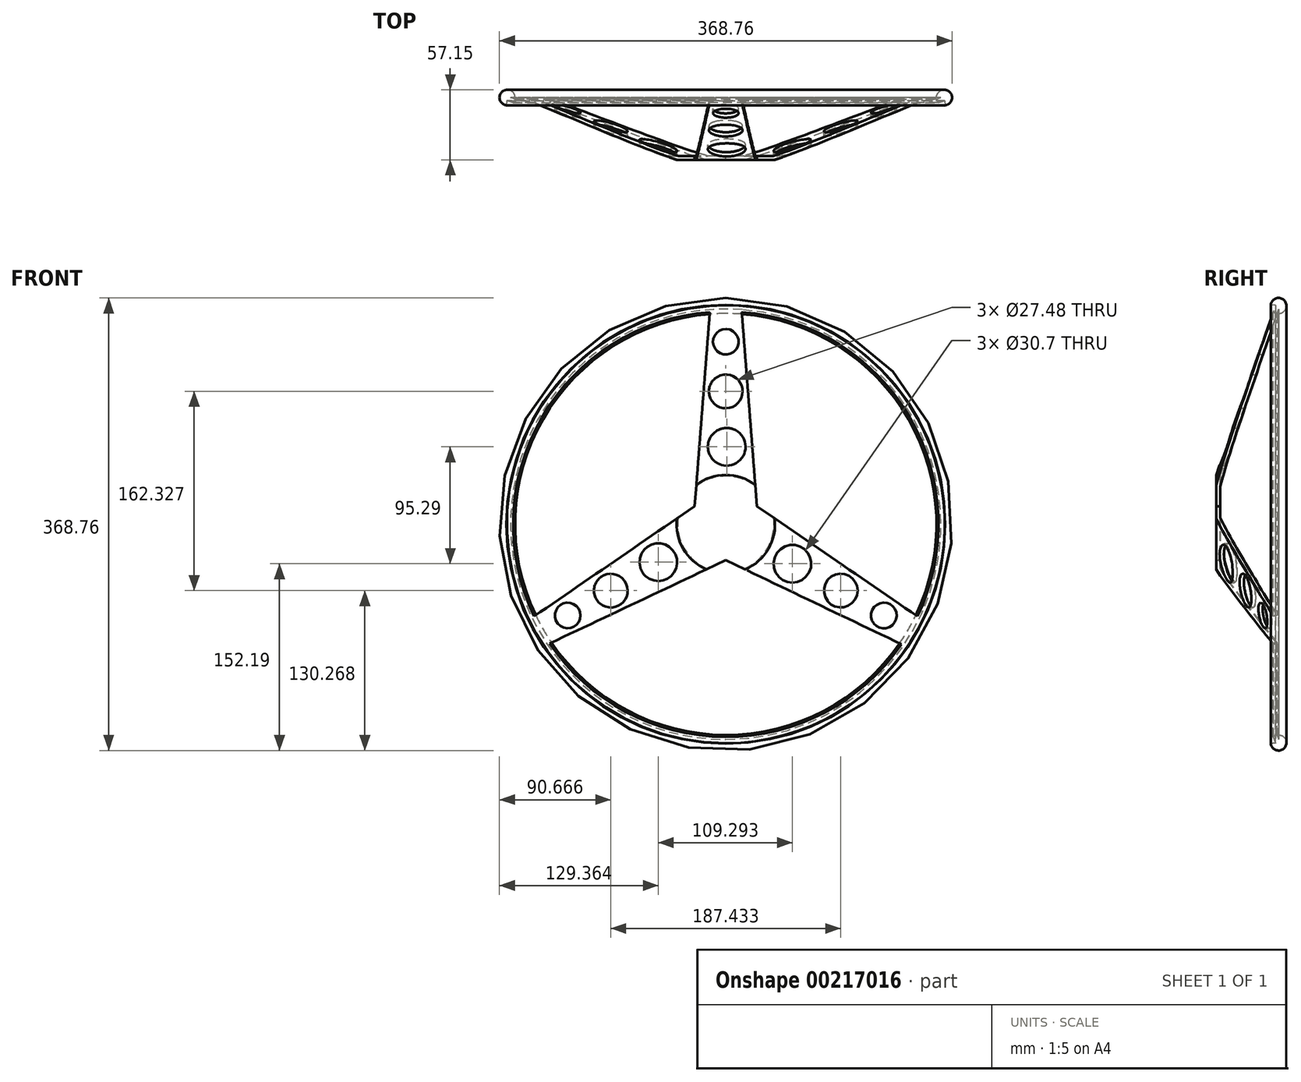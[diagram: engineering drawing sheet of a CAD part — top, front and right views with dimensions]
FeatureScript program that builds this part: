
annotation { "Feature Type Name" : "Feature", "Feature Type Description" : "" }
export const myFeature = defineFeature(function(context is Context, id is Id, definition is map)
    precondition{}
    {
        {
            var Q0;
            Q0=qCreatedBy(makeId("Front.planeOp"),FACE);
            var sketch = newSketch(context, id + "F0", { "sketchPlane" : qUnion([Q0])});
            skCircle(sketch, "E0", {"center": v(0, 0) * mm, "radius": 177.8 * mm});
            skLineSegment(sketch, "E1.1", {"start": v(139.7, -109.99) * mm, "end": v(141.28, -110.9) * mm});
            skLineSegment(sketch, "E2", {"start": v(-159.95, -77.64) * mm, "end": v(-25.4, 14.66) * mm});
            skLineSegment(sketch, "E3", {"start": v(-147.63, -99.09) * mm, "end": v(0, -29.33) * mm});
            skPoint(sketch, "E3.startSnap0", {"position": v(-147.63, -99.9) * mm});
            skLineSegment(sketch, "E4", {"start": v(159.95, -77.64) * mm, "end": v(25.4, 14.66) * mm});
            skLineSegment(sketch, "E5", {"start": v(0, -29.33) * mm, "end": v(147.22, -99.7) * mm});
            skLineSegment(sketch, "E6", {"start": v(-12.7, 177.8) * mm, "end": v(-25.4, 14.66) * mm});
            skLineSegment(sketch, "E7", {"start": v(12.74, 177.34) * mm, "end": v(25.4, 14.66) * mm});
            skPoint(sketch, "E8.1.end.orphan", {"position": v(-25.4, 177.8) * mm});
            skPoint(sketch, "E9.orphan", {"position": v(25.4, 177.8) * mm});
            skPoint(sketch, "E10.start.orphan", {"position": v(12.7, 177.8) * mm});
            skPoint(sketch, "E11.1.end.orphan", {"position": v(166.68, -66.9) * mm});
            skPoint(sketch, "E12.orphan", {"position": v(160.33, -77.9) * mm});
            skPoint(sketch, "E13.orphan", {"position": v(147.63, -99.9) * mm});
            skPoint(sketch, "E1.0.end.orphan", {"position": v(-141.28, -110.9) * mm});
            skPoint(sketch, "E14.orphan", {"position": v(-160.33, -77.9) * mm});
            skPoint(sketch, "E8.0.end.orphan", {"position": v(-166.68, -66.9) * mm});
            skPoint(sketch, "E15.end.orphan", {"position": v(0, 177.8) * mm});
            skPoint(sketch, "E16.end.orphan", {"position": v(-153.98, -88.9) * mm});
            skPoint(sketch, "E17.end.orphan", {"position": v(153.98, -88.9) * mm});
            skCircle(sketch, "E18", {"center": v(0, 0) * mm, "radius": 29.33 * mm});
            skSolve(sketch);
        }
        {
            var Q0;
            {var subQ0=sQuery(id+"F0.wireOp",EDGE,"E2");Q0=makeQuery(id+"F0.imprint","IMPRINT",FACE,{"disambiguationData":[TD([[makeQuery(id+"F0.imprint","IMPRINT",EDGE,{"derivedFrom":subQ0}),-1.0]])]});}
            var Q1;
            {var subQ0=sQuery(id+"F0.wireOp",EDGE,"E7");Q1=makeQuery(id+"F0.imprint","IMPRINT",FACE,{"disambiguationData":[TD([[makeQuery(id+"F0.imprint","IMPRINT",EDGE,{"derivedFrom":subQ0}),-1.0]])]});}
            var Q2;
            {var subQ0=sQuery(id+"F0.wireOp",EDGE,"E4");Q2=makeQuery(id+"F0.imprint","IMPRINT",FACE,{"disambiguationData":[TD([[makeQuery(id+"F0.imprint","IMPRINT",EDGE,{"derivedFrom":subQ0}),1.0]])]});}
            var Q3;
            {var subQ0=sQuery(id+"F0.wireOp",EDGE,"E18");var subQ1=makeQuery(id+"F0.imprint","INTERSECT",VERTEX,{"derivedFrom":[sQuery(id+"F0.wireOp",EDGE,"E2"),sQuery(id+"F0.wireOp",EDGE,"E6"),subQ0]});Q3=makeQuery(id+"F0.imprint","IMPRINT",FACE,{"disambiguationData":[TD([[makeQuery(id+"F0.imprint","IMPRINT",EDGE,{"disambiguationData":[TD([[subQ1,1.0]])],"derivedFrom":subQ0}),1.0]])]});}
            extrude(context, id + "F1", {"entities" : qUnion([Q0, Q1, Q2, Q3]), "depth" : 50.8 * mm});
        }
        {
            var Q0;
            Q0=qCreatedBy(makeId("Right.planeOp"),FACE);
            var sketch = newSketch(context, id + "F2", { "sketchPlane" : qUnion([Q0])});
            skCircle(sketch, "E19", {"center": v(0, 178.03) * mm, "radius": 6.35 * mm});
            skSolve(sketch);
        }
        {
            var Q0;
            Q0 = qSketchRegion(id + "F2", true);
            var Q1;
            {var subQ0=sQuery(id+"F0.wireOp",EDGE,"E0");Q1=makeQuery(id+"F1.opExtrude","SWEPT_FACE",FACE,{"disambiguationData":[OSD([subQ0]),TDD([makeQuery(id+"F0.imprint","IMPRINT",EDGE,{"disambiguationData":[TD([[makeQuery(id+"F0.imprint","INTERSECT",VERTEX,{"derivedFrom":[subQ0,sQuery(id+"F0.wireOp",EDGE,"E7")]}),-1.0]])],"derivedFrom":subQ0})])]});}
            revolve(context, id + "F3", {"operationType" : NewBodyOperationType.ADD, "entities" : qUnion([Q0]), "axis" : qUnion([Q1]), "revolveType" : RevolveType.FULL});
        }
        {
            var Q0;
            Q0=qCreatedBy(makeId("Right.planeOp"),FACE);
            var sketch = newSketch(context, id + "F4", { "sketchPlane" : qUnion([Q0])});
            skLineSegment(sketch, "E20", {"start": v(0, 178.42) * mm, "end": v(-2.42, 178.42) * mm});
            skLineSegment(sketch, "E21", {"start": v(-2.42, 178.42) * mm, "end": v(-50.73, 40.03) * mm});
            skLineSegment(sketch, "E22", {"start": v(-50.73, 40.03) * mm, "end": v(-69.71, 57.98) * mm});
            skLineSegment(sketch, "E23", {"start": v(-69.71, 57.98) * mm, "end": v(-64.88, 183.6) * mm});
            skLineSegment(sketch, "E24", {"start": v(-64.88, 183.6) * mm, "end": v(-2.42, 178.42) * mm});
            skLineSegment(sketch, "E25", {"start": v(0, 175.31) * mm, "end": v(-47.51, 39.22) * mm});
            skLineSegment(sketch, "E26", {"start": v(-47.51, 39.22) * mm, "end": v(-47.51, 0) * mm});
            skLineSegment(sketch, "E27", {"start": v(-47.51, 0) * mm, "end": v(0, 0) * mm});
            skLineSegment(sketch, "E28", {"start": v(0, 0) * mm, "end": v(0, 175.31) * mm});
            skSolve(sketch);
        }
        {
            var Q0;
            Q0=makeQuery(id+"F1.opExtrude","CAP_FACE",FACE,{"disambiguationData":[OSD([sQuery(id+"F0.wireOp",EDGE,"E0"),sQuery(id+"F0.wireOp",EDGE,"E2"),sQuery(id+"F0.wireOp",EDGE,"E3"),sQuery(id+"F0.wireOp",EDGE,"E4"),sQuery(id+"F0.wireOp",EDGE,"E5"),sQuery(id+"F0.wireOp",EDGE,"E6"),sQuery(id+"F0.wireOp",EDGE,"E7")])],"isStart":true});
            var sketch = newSketch(context, id + "F5", { "sketchPlane" : qUnion([Q0])});
            skCircle(sketch, "E29", {"center": v(0, 0) * mm, "radius": 27.58 * mm});
            skSolve(sketch);
        }
        {
            var Q0;
            Q0 = qSketchRegion(id + "F5", true);
            extrude(context, id + "F6", {"entities" : qUnion([Q0]), "operationType" : NewBodyOperationType.REMOVE, "oppositeDirection" : true, "depth" : 44.45 * mm});
        }
        {
            var Q0;
            Q0 = qSketchRegion(id + "F4", true);
            var Q1;
            Q1=makeQuery(id+"F3.opRevolve","SWEPT_FACE",FACE,{"disambiguationData":[OSD([sQuery(id+"F2.wireOp",EDGE,"E19")])]});
            revolve(context, id + "F7", {"operationType" : NewBodyOperationType.REMOVE, "entities" : qUnion([Q0]), "axis" : qUnion([Q1]), "revolveType" : RevolveType.FULL, "oppositeDirection" : true});
        }
        {
            var Q0;
            Q0=qCreatedBy(makeId("Front.planeOp"),FACE);
            var sketch = newSketch(context, id + "F8", { "sketchPlane" : qUnion([Q0])});
            skCircle(sketch, "E30", {"center": v(0, 0) * mm, "radius": 38.86 * mm});
            skCircle(sketch, "E31", {"center": v(54.28, -32.19) * mm, "radius": 15.35 * mm});
            skCircle(sketch, "E32", {"center": v(93.72, -54.1) * mm, "radius": 13.74 * mm});
            skCircle(sketch, "E33", {"center": v(128.78, -74.37) * mm, "radius": 10.42 * mm});
            skCircle(sketch, "E34.1.1", {"center": v(0.74, 63.1) * mm, "radius": 15.35 * mm});
            skCircle(sketch, "E34.1.2", {"center": v(0, 108.21) * mm, "radius": 13.74 * mm});
            skCircle(sketch, "E34.1.3", {"center": v(0.02, 148.71) * mm, "radius": 10.42 * mm});
            skCircle(sketch, "E34.2.1", {"center": v(-55.02, -30.91) * mm, "radius": 15.35 * mm});
            skCircle(sketch, "E34.2.2", {"center": v(-93.71, -54.11) * mm, "radius": 13.74 * mm});
            skCircle(sketch, "E34.2.3", {"center": v(-128.8, -74.34) * mm, "radius": 10.42 * mm});
            skSolve(sketch);
        }
        {
            var Q0;
            Q0=makeQuery(id+"F8.imprint","IMPRINT",FACE,{"disambiguationData":[TD([[makeQuery(id+"F8.imprint","IMPRINT",EDGE,{"derivedFrom":sQuery(id+"F8.wireOp",EDGE,"E34.1.3")}),1.0]])]});
            var Q1;
            Q1=makeQuery(id+"F8.imprint","IMPRINT",FACE,{"disambiguationData":[TD([[makeQuery(id+"F8.imprint","IMPRINT",EDGE,{"derivedFrom":sQuery(id+"F8.wireOp",EDGE,"E34.1.2")}),1.0]])]});
            var Q2;
            Q2=makeQuery(id+"F8.imprint","IMPRINT",FACE,{"disambiguationData":[TD([[makeQuery(id+"F8.imprint","IMPRINT",EDGE,{"derivedFrom":sQuery(id+"F8.wireOp",EDGE,"E34.1.1")}),1.0]])]});
            var Q3;
            Q3=makeQuery(id+"F8.imprint","IMPRINT",FACE,{"disambiguationData":[TD([[makeQuery(id+"F8.imprint","IMPRINT",EDGE,{"derivedFrom":sQuery(id+"F8.wireOp",EDGE,"E34.2.3")}),1.0]])]});
            var Q4;
            Q4=makeQuery(id+"F8.imprint","IMPRINT",FACE,{"disambiguationData":[TD([[makeQuery(id+"F8.imprint","IMPRINT",EDGE,{"derivedFrom":sQuery(id+"F8.wireOp",EDGE,"E34.2.2")}),1.0]])]});
            var Q5;
            Q5=makeQuery(id+"F8.imprint","IMPRINT",FACE,{"disambiguationData":[TD([[makeQuery(id+"F8.imprint","IMPRINT",EDGE,{"derivedFrom":sQuery(id+"F8.wireOp",EDGE,"E34.2.1")}),1.0]])]});
            var Q6;
            Q6=makeQuery(id+"F8.imprint","IMPRINT",FACE,{"disambiguationData":[TD([[makeQuery(id+"F8.imprint","IMPRINT",EDGE,{"derivedFrom":sQuery(id+"F8.wireOp",EDGE,"E31")}),1.0]])]});
            var Q7;
            Q7=makeQuery(id+"F8.imprint","IMPRINT",FACE,{"disambiguationData":[TD([[makeQuery(id+"F8.imprint","IMPRINT",EDGE,{"derivedFrom":sQuery(id+"F8.wireOp",EDGE,"E32")}),1.0]])]});
            var Q8;
            Q8=makeQuery(id+"F8.imprint","IMPRINT",FACE,{"disambiguationData":[TD([[makeQuery(id+"F8.imprint","IMPRINT",EDGE,{"derivedFrom":sQuery(id+"F8.wireOp",EDGE,"E33")}),1.0]])]});
            extrude(context, id + "F9", {"entities" : qUnion([Q0, Q1, Q2, Q3, Q4, Q5, Q6, Q7, Q8]), "operationType" : NewBodyOperationType.REMOVE, "endBound" : BoundingType.THROUGH_ALL, "depth" : 25.4 * mm});
        }
    });
